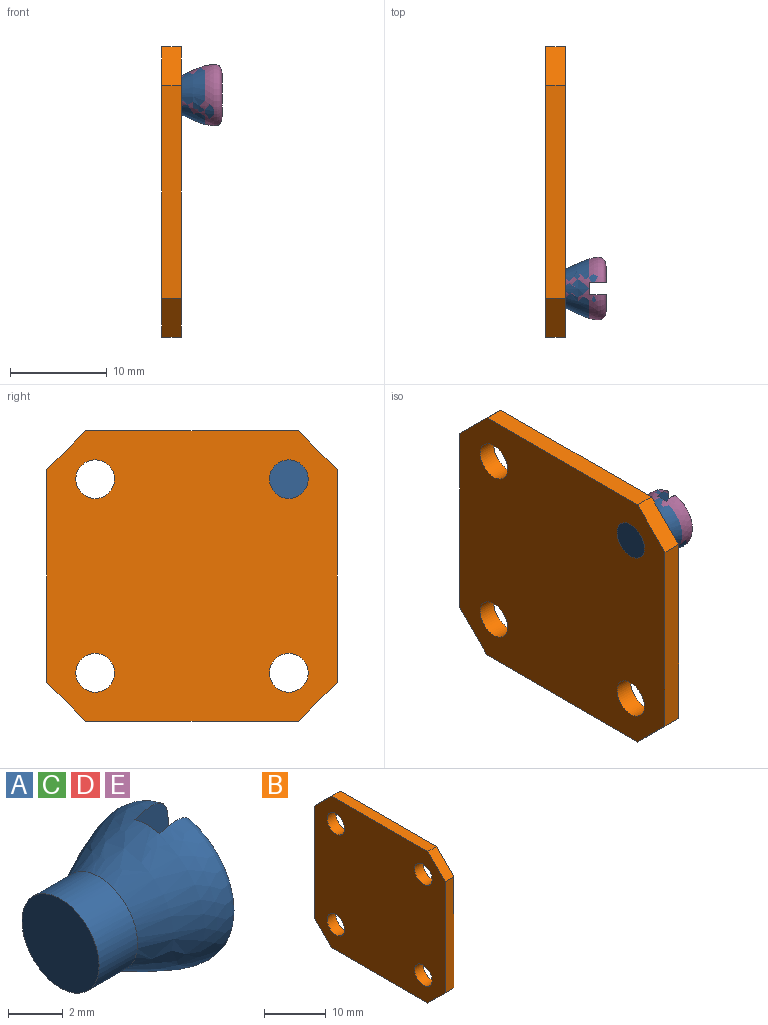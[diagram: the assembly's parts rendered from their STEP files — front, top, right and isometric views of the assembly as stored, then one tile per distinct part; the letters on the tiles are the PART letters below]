
ASSEMBLY  parts=5 mates=1
PART A: 6 faces, bbox 6.7x8.5x8.5 mm
  f0: bspline ~8.51x8.51mm, area 92.6mm2, adj f1,f3,f4,f5
  f1: cylinder r=2mm len=4mm, axis (1,0,0), area 25.1mm2, adj f0,f2
  f2: plane 4x4mm, normal (-1,0,0), area 12.6mm2, adj f1
  f3: plane 6.34x1.74mm, normal (0,1,0), area 10.3mm2, adj f0,f5
  f4: plane 6.34x1.74mm, normal (0,-1,0), area 10.3mm2, adj f0,f5
  f5: plane 6.16x1.3mm, normal (1,0,0), area 7.9mm2, adj f0,f3,f4
PART B: 14 faces, bbox 2x30x30 mm
  f0: plane 22x2mm, normal (0,0,1), area 44mm2, adj f4,f5,f12,f13
  f1: plane 22x2mm, normal (0,-1,0), area 44mm2, adj f4,f5,f10,f13
  f2: plane 22x2mm, normal (0,0,-1), area 44mm2, adj f4,f5,f10,f11
  f3: plane 22x2mm, normal (0,1,0), area 44mm2, adj f4,f5,f11,f12
  f4: plane 30x30mm, normal (1,0,0), area 817.7mm2, adj f0,f1,f2,f3,f6,f7,f8,f9
  f5: plane 30x30mm, normal (-1,0,0), area 817.7mm2, adj f0,f1,f2,f3,f6,f7,f8,f9
  f6: cylinder r=2mm len=4mm, axis (1,0,0), area 25.1mm2, adj f4,f5
  f7: cylinder r=2mm len=4mm, axis (1,0,0), area 25.1mm2, adj f4,f5
  f8: cylinder r=2mm len=4mm, axis (1,0,0), area 25.1mm2, adj f4,f5
  f9: cylinder r=2mm len=4mm, axis (1,0,0), area 25.1mm2, adj f4,f5
  f10: plane 4x4mm, normal (0,-0.71,-0.71), area 11.3mm2, adj f1,f2,f4,f5
  f11: plane 4x4mm, normal (0,0.71,-0.71), area 11.3mm2, adj f2,f3,f4,f5
  f12: plane 4x4mm, normal (0,0.71,0.71), area 11.3mm2, adj f0,f3,f4,f5
  f13: plane 4x4mm, normal (0,-0.71,0.71), area 11.3mm2, adj f0,f1,f4,f5
PART C: same geometry as A
PART D: same geometry as A
PART E: same geometry as A
PLACE A t=(-28.06,-7.2,1.09)mm
PLACE B t=(-29.06,2.8,-8.91)mm
PLACE C t=(-28.06,-7.2,1.09)mm
PLACE D t=(-28.06,-7.2,1.09)mm
PLACE E t=(-28.06,-7.2,1.09)mm
MATE revolute D.f1 <-> B.f6  axis (-1,0,0) through (-30.06,-7.2,1.09)mm
